# Revit family: IS_Mara_A9029_BIM_IT
name_source: partatom
category: Plumbing Fixtures
revit_build: Autodesk Revit MEP 2016 (Build: 20161004_0715(x64)
units: mm (PartAtom-declared; Revit-internal decimal feet)

## family parameters
Always vertical = No
Cut with Voids When Loaded = No
OmniClass Number = 23.45.55.17
OmniClass Title = Mixing Faucets
Part Type = Normal
Room Calculation Point = No
Round Connector Dimension = Use Diameter
Shared = No
Work Plane-Based = No

## types (1)
- A9029AA - MARA MISC LVB BOCCA ALTA H221MM CR
    Accessori = www.idealstandard.it
    AltezzaNominale = 288 mm
    Assembly Code = C1030200
    Autore = Ideal Standard Italia
    BIMobject category = Taps & Mixers
    BOSUseNativeGeometries = 1
    Brand = Ideal Standard
    Brand url = http://www.idealstandard.co.uk
    Caratteristiche = Miscelatore monocomando lavabo a bocca alta, con bocca di erogazione orientabile, aeratore nascosto e tubi flessibili. Dotato di cartuccia da 35 mm con limitatore della temperatura. Sistema di fissaggio Easy Fix. Sporgenza bocca 100 mm, altezza bocca 211 mm. Altezza totale tubo 288 mm. Con asta di comando e piletta cromata da 1-1/4”.
    CodiceABarre = 3800861018070
    Colore = Cromato
    Connessione = Installazione
    CostoDiSostituzione = 0 $
    Description = MARA - Miscelatore monocomando lavabo a bocca alta, con bocca di erogazione orientabile, aeratore nascosto e tubi flessibili. Dotato di cartuccia da 35 mm con limitatore della temperatura. Sistema di fissaggio Easy Fix. Sporgenza bocca 100 mm, altezza bocca 211 mm. Altezza totale tubo 288 mm. Con asta di comando e piletta cromata da 1-1/4”.
    DescrizioneClassifcazioneUni2015 = Washbasin taps ?
    Dimensione = 288 x 87 x 135
    DurataGaranziaProdotti = 5
    EAN code = https://3800861018070
    Edition number = 1
    Finitura = Cromato
    Garanzia = Garanzia Idealstandard
    IFC Classification = Sanitary Terminal
    InformazioniDiProdotto = www.idealstandard.it/prodotti/html
    InformazioniGaranzia = www.idealstandard.it/garanzia.html
    Installation instructions = www.idealstandard.it/prodotti/html
    InstruzioniInstallazione = www.idealstandard.it/prodotti/html
    LarghezzaNominale = 87 mm
    LunghezzaNominale = 135 mm
    Manufacturer = www.idealstandard.it
    Manufacturer name = Ideal Standard
    Material main = Brass
    Materiale = Ottone
    Model = A9029AA
    NBS Reference Code = 35-79-95
    NBS Reference Description = Wash Basin And Trough Water Supply Fittings
    Nominal height = 131
    Nominal width = 79
    NumeroDiModello = A9029AA
    OmniClass Code = 23-31 11 00
    OmniClass Description = Faucets
    PesoNetto = 2,517 KG
    Product Guid = 75edc25d-ff55-4032-b635-743c5cb1aead
    Product SKU = A9029
    Product certification = http://www.idealstandard.it
    Product data url = https://bimobject.com
    Product family = MARA
    Product group = Basin Mixer
    Product name = MARA BASIN MIXER R-MTD T.SPT R100 PUW SPX3/8
    Product url = http://www.idealstandard.it
    QR code = http://bimobject.com
    Revisione = 1
    RiferimentoClassificazioneUni2015 = Pr_40_20_87_98
    Spazio = Interno
    Technical description = www.idealstandard.it/prodotti/html
    Telefono = 800 652 290
    URL = www.idealstandard.it
    Uniclass 1.4 Code = L8212
    Uniclass 1.4 Description = Fittings
    Uniclass 2.0 Code = PR-35-79-95
    Uniclass 2.0 Description = Wash Basin And Trough Water Supply Fittings
    Uniclass 2015 Code = Pr_40_20_87_96
    Uniclass 2015 Name = Washbasin manual water supply sets
    UnitaDurata = anni
    UnitaDurataGaranzia = anni
    UnitaLineare = milimetri
    UnitaVolume = Litri
    Versione = 1
    VersioneClassificazioneUni2015 = Products v1.1
    Weight Net (Kg) = 2.52

## geometry (parser evidence)
native form markers: Blend x4, Sweep x1
no freeform markers — native parametric forms only
